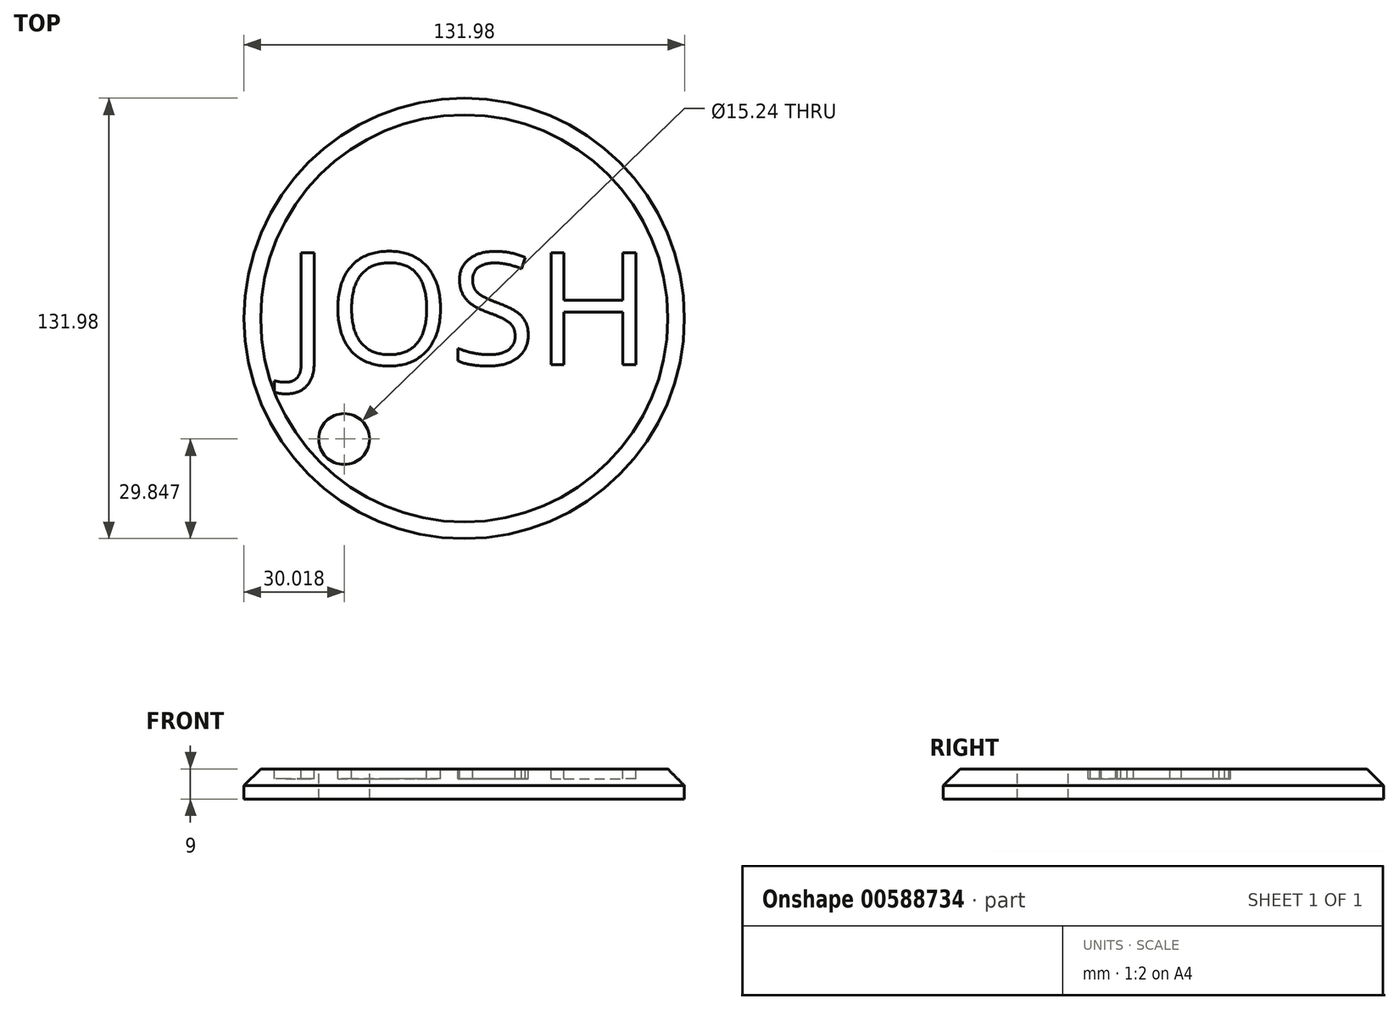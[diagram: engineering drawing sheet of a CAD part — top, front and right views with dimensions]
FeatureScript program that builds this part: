
annotation { "Feature Type Name" : "Feature", "Feature Type Description" : "" }
export const myFeature = defineFeature(function(context is Context, id is Id, definition is map)
    precondition{}
    {
        {
            var Q0;
            Q0=qCreatedBy(makeId("Top.planeOp"),FACE);
            var sketch = newSketch(context, id + "F0", { "sketchPlane" : qUnion([Q0])});
            skCircle(sketch, "E0", {"center": v(2.67, 0) * mm, "radius": 66 * mm});
            skSolve(sketch);
        }
        {
            var Q0;
            Q0=makeQuery(id+"F0.imprint","IMPRINT",FACE,{"disambiguationData":[TD([[makeQuery(id+"F0.imprint","IMPRINT",EDGE,{"derivedFrom":sQuery(id+"F0.wireOp",EDGE,"E0")}),1.0]])]});
            extrude(context, id + "F1", {"entities" : qUnion([Q0]), "depth" : 9 * mm, "offsetDistance" : 25.4 * mm});
        }
        {
            var Q0;
            Q0=makeQuery(id+"F1.opExtrude","CAP_FACE",FACE,{"disambiguationData":[OSD([sQuery(id+"F0.wireOp",EDGE,"E0")])],"isStart":false});
            chamfer(context, id + "F2", {"entities" : qUnion([Q0]), "width" : 5 * mm, "tangentPropagation" : true});
        }
        {
            var Q0;
            Q0=makeQuery(id+"F1.opExtrude","CAP_FACE",FACE,{"disambiguationData":[OSD([sQuery(id+"F0.wireOp",EDGE,"E0")])],"isStart":false});
            var sketch = newSketch(context, id + "F3", { "sketchPlane" : qUnion([Q0])});
            skSolve(sketch);
        }
        {
            var Q0;
            {var subQ0=sQuery(id+"F0.wireOp",EDGE,"E0");Q0=makeQuery(id+"F3.imprint","IMPRINT",FACE,{"disambiguationData":[TD([[makeQuery(id+"F3.imprint","IMPRINT",EDGE,{"derivedFrom":makeQuery(id+"F2.opChamfer","BLEND_EDGE",EDGE,{"blendedFrom":[makeQuery(id+"F1.opExtrude","CAP_EDGE",EDGE,{"disambiguationData":[OSD([subQ0])],"isStart":false}),makeQuery(id+"F1.opExtrude","CAP_FACE",FACE,{"disambiguationData":[OSD([subQ0])],"isStart":false})],"blendedInto":[makeQuery(id+"F1.opExtrude","CAP_FACE",FACE,{"disambiguationData":[OSD([subQ0])],"isStart":false})]})}),1.0]])]});}
            var sketch = newSketch(context, id + "F4", { "sketchPlane" : qUnion([Q0])});
            skText(sketch, "E1", { "text": "JOSH\n", "fontName": "OpenSans-Regular.ttf"});
            const initialGuessF4  = {"E1": [-0.05054, -0.01381, 1, 0, 0.0337]};
            skSetInitialGuess(sketch, initialGuessF4);
            skSolve(sketch);
        }
        {
            var Q0;
            Q0 = qSketchRegion(id + "F4", true);
            extrude(context, id + "F5", {"entities" : qUnion([Q0]), "operationType" : NewBodyOperationType.REMOVE, "oppositeDirection" : true, "depth" : 3 * mm, "offsetDistance" : 25 * mm});
        }
        {
            var Q0;
            {var subQ0=sQuery(id+"F0.wireOp",EDGE,"E0");Q0=makeQuery(id+"F3.imprint","IMPRINT",FACE,{"disambiguationData":[TD([[makeQuery(id+"F3.imprint","IMPRINT",EDGE,{"derivedFrom":makeQuery(id+"F2.opChamfer","BLEND_EDGE",EDGE,{"blendedFrom":[makeQuery(id+"F1.opExtrude","CAP_EDGE",EDGE,{"disambiguationData":[OSD([subQ0])],"isStart":false}),makeQuery(id+"F1.opExtrude","CAP_FACE",FACE,{"disambiguationData":[OSD([subQ0])],"isStart":false})],"blendedInto":[makeQuery(id+"F1.opExtrude","CAP_FACE",FACE,{"disambiguationData":[OSD([subQ0])],"isStart":false})]})}),1.0]])]});}
            var sketch = newSketch(context, id + "F6", { "sketchPlane" : qUnion([Q0])});
            skCircle(sketch, "E2", {"center": v(-33.3, -36.14) * mm, "radius": 7.62 * mm});
            skSolve(sketch);
        }
        {
            var Q0;
            Q0 = qSketchRegion(id + "F6", true);
            extrude(context, id + "F7", {"entities" : qUnion([Q0]), "operationType" : NewBodyOperationType.REMOVE, "oppositeDirection" : true, "depth" : 9 * mm, "offsetDistance" : 25 * mm});
        }
    });
